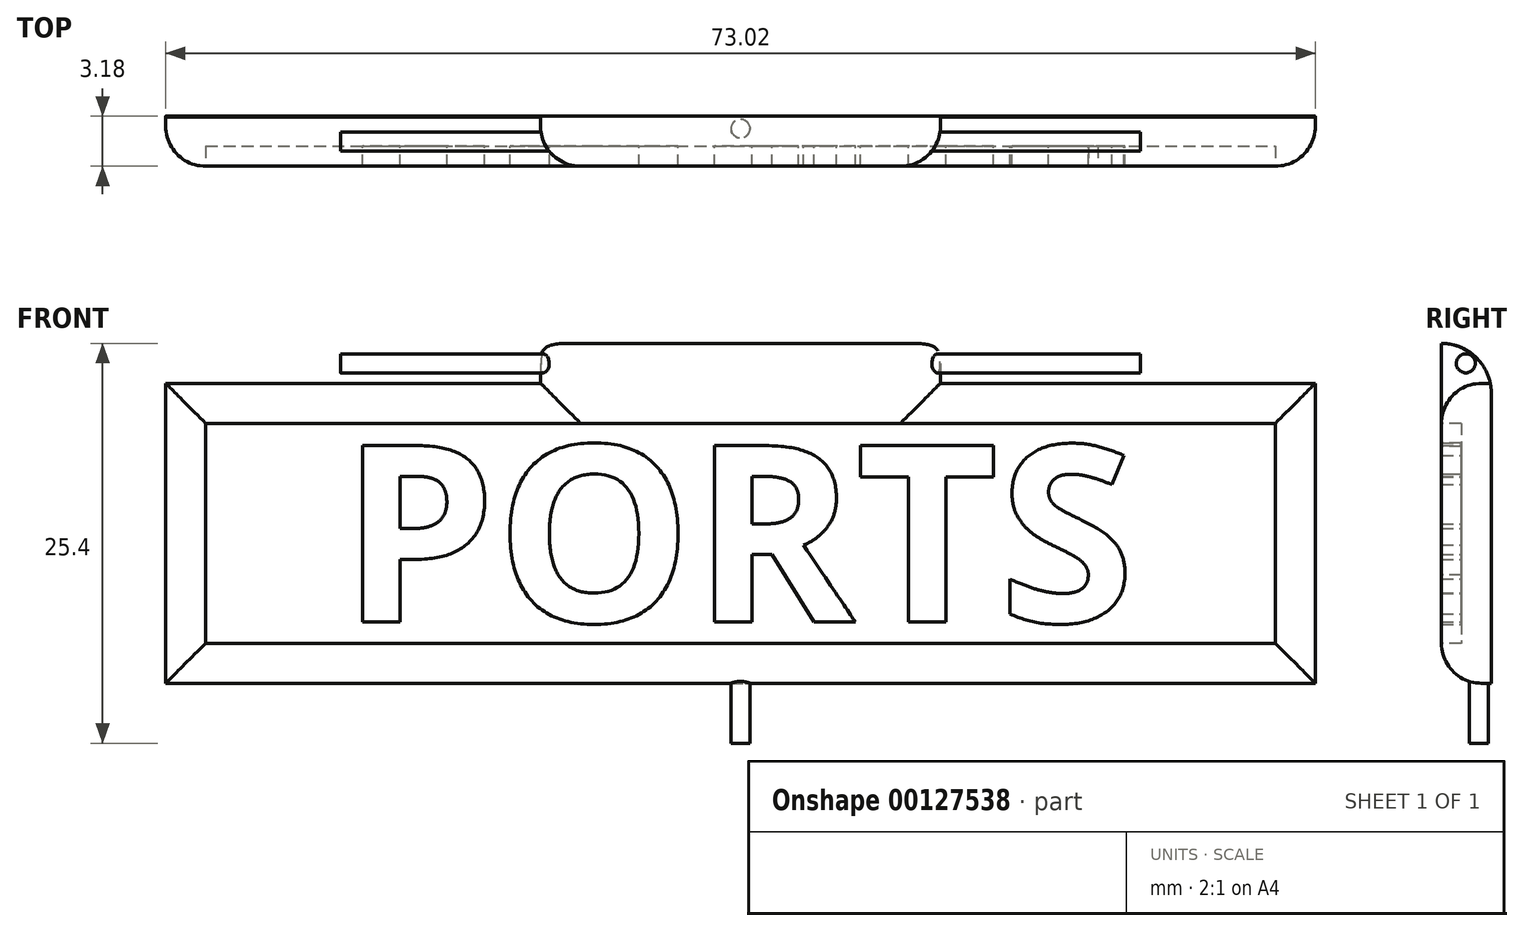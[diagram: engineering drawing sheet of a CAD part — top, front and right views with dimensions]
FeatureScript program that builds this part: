
annotation { "Feature Type Name" : "Feature", "Feature Type Description" : "" }
export const myFeature = defineFeature(function(context is Context, id is Id, definition is map)
    precondition{}
    {
        {
            var Q0;
            Q0=qCreatedBy(makeId("Front.planeOp"),FACE);
            var sketch = newSketch(context, id + "F0", { "sketchPlane" : qUnion([Q0])});
            skLineSegment(sketch, "E0.bottom", {"start": v(-57.71, 18) * mm, "end": v(15.31, 18) * mm});
            skLineSegment(sketch, "E0.top", {"start": v(-57.71, -1.06) * mm, "end": v(15.31, -1.06) * mm});
            skLineSegment(sketch, "E0.left", {"start": v(-57.71, 18) * mm, "end": v(-57.71, -1.06) * mm});
            skLineSegment(sketch, "E0.right", {"start": v(15.31, 18) * mm, "end": v(15.31, -1.06) * mm});
            skSolve(sketch);
        }
        {
            var Q0;
            Q0 = qSketchRegion(id + "F0", true);
            extrude(context, id + "F1", {"entities" : qUnion([Q0]), "depth" : 3.17 * mm});
        }
        {
            var Q0;
            Q0=makeQuery(id+"F1.opExtrude","SWEPT_FACE",FACE,{"disambiguationData":[OSD([sQuery(id+"F0.wireOp",EDGE,"E0.top")])]});
            var sketch = newSketch(context, id + "F2", { "sketchPlane" : qUnion([Q0])});
            skLineSegment(sketch, "E1", {"start": v(-57.71, 1.59) * mm, "end": v(-57.71, 0) * mm});
            skCircle(sketch, "E2", {"center": v(-21.2, 0.8) * mm, "radius": 0.6 * mm});
            skPoint(sketch, "E2.centerSnap0", {"position": v(-21.2, 0) * mm});
            skPoint(sketch, "E2.centerSnap1", {"position": v(-57.71, 0.8) * mm});
            skSolve(sketch);
        }
        {
            var Q0;
            Q0 = qSketchRegion(id + "F2", true);
            extrude(context, id + "F3", {"entities" : qUnion([Q0]), "operationType" : NewBodyOperationType.ADD, "depth" : 3.8 * mm});
        }
        {
            var Q0;
            Q0=makeQuery(id+"F1.opExtrude","SWEPT_FACE",FACE,{"disambiguationData":[OSD([sQuery(id+"F0.wireOp",EDGE,"E0.bottom")])]});
            var sketch = newSketch(context, id + "F4", { "sketchPlane" : qUnion([Q0])});
            skLineSegment(sketch, "E3.bottom", {"start": v(-33.9, -3.18) * mm, "end": v(-8.5, -3.18) * mm});
            skLineSegment(sketch, "E3.top", {"start": v(-33.9, 0) * mm, "end": v(-8.5, 0) * mm});
            skLineSegment(sketch, "E3.left", {"start": v(-33.9, -3.18) * mm, "end": v(-33.9, 0) * mm});
            skLineSegment(sketch, "E3.right", {"start": v(-8.5, -3.18) * mm, "end": v(-8.5, 0) * mm});
            skPoint(sketch, "E3.middle", {"position": v(-21.2, -1.59) * mm});
            skPoint(sketch, "E3.middle.positionSnap0", {"position": v(-21.2, -3.18) * mm});
            skPoint(sketch, "E3.middle.positionSnap1", {"position": v(15.31, -1.59) * mm});
            skPoint(sketch, "E3.centerSnap0", {"position": v(-21.2, -3.18) * mm});
            skPoint(sketch, "E3.centerSnap1", {"position": v(15.31, -1.59) * mm});
            skSolve(sketch);
        }
        {
            var Q0;
            Q0=makeQuery(id+"F4.imprint","IMPRINT",FACE,{"disambiguationData":[TD([[makeQuery(id+"F4.imprint","IMPRINT",EDGE,{"derivedFrom":sQuery(id+"F4.wireOp",EDGE,"E3.bottom")}),1.0]])]});
            extrude(context, id + "F5", {"entities" : qUnion([Q0]), "operationType" : NewBodyOperationType.ADD, "depth" : 2.54 * mm});
        }
        {
            var Q0;
            Q0=makeQuery(id+"F5.opExtrude","CAP_EDGE",EDGE,{"disambiguationData":[OSD([sQuery(id+"F4.wireOp",EDGE,"E3.top")])],"isStart":false});
            fillet(context, id + "F6", {"entities" : qUnion([Q0]), "radius" : 3.17 * mm, "tangentPropagation" : true, "allowEdgeOverflow" : false});
        }
        {
            var Q0;
            Q0=makeQuery(id+"F5.opExtrude","SWEPT_FACE",FACE,{"disambiguationData":[OSD([sQuery(id+"F4.wireOp",EDGE,"E3.right")])]});
            var sketch = newSketch(context, id + "F7", { "sketchPlane" : qUnion([Q0])});
            skCircle(sketch, "E4", {"center": v(-1.62, 19.26) * mm, "radius": 0.6 * mm});
            skPoint(sketch, "E4.centerSnap0", {"position": v(-1.62, 18) * mm});
            skPoint(sketch, "E4.centerSnap1", {"position": v(-3.18, 19.26) * mm});
            skSolve(sketch);
        }
        {
            var Q0;
            Q0 = qSketchRegion(id + "F7", true);
            extrude(context, id + "F8", {"entities" : qUnion([Q0]), "operationType" : NewBodyOperationType.ADD, "depth" : 12.7 * mm});
        }
        {
            var Q0;
            Q0=makeQuery(id+"F5.opExtrude","SWEPT_FACE",FACE,{"disambiguationData":[OSD([sQuery(id+"F4.wireOp",EDGE,"E3.left")])]});
            var sketch = newSketch(context, id + "F9", { "sketchPlane" : qUnion([Q0])});
            skCircle(sketch, "E5", {"center": v(1.62, 19.26) * mm, "radius": 0.6 * mm});
            skPoint(sketch, "E5.centerSnap0", {"position": v(1.62, 18) * mm});
            skPoint(sketch, "E5.centerSnap1", {"position": v(3.18, 19.26) * mm});
            skSolve(sketch);
        }
        {
            var Q0;
            Q0 = qSketchRegion(id + "F9", true);
            extrude(context, id + "F10", {"entities" : qUnion([Q0]), "operationType" : NewBodyOperationType.ADD, "depth" : 12.7 * mm});
        }
        {
            var Q0;
            Q0=makeQuery(id+"F1.opExtrude","CAP_EDGE",EDGE,{"disambiguationData":[OSD([sQuery(id+"F0.wireOp",EDGE,"E0.top")])],"isStart":false});
            var Q1;
            Q1=makeQuery(id+"F1.opExtrude","CAP_EDGE",EDGE,{"disambiguationData":[OSD([sQuery(id+"F0.wireOp",EDGE,"E0.right")])],"isStart":false});
            var Q2;
            {var subQ0=sQuery(id+"F0.wireOp",EDGE,"E0.right");var subQ1=sQuery(id+"F0.wireOp",EDGE,"E0.bottom");Q2=makeQuery(id+"F5.boolean.opBoolean","SPLIT",EDGE,{"disambiguationData":[TD([makeQuery(id+"F1.opExtrude","SWEPT_FACE",FACE,{"disambiguationData":[OSD([subQ0])]})])],"derivedFrom":makeQuery(id+"F1.opExtrude","CAP_EDGE",EDGE,{"disambiguationData":[OSD([subQ1])],"isStart":false})});}
            var Q3;
            Q3=makeQuery(id+"F1.opExtrude","CAP_EDGE",EDGE,{"disambiguationData":[OSD([sQuery(id+"F0.wireOp",EDGE,"E0.left")])],"isStart":false});
            var Q4;
            {var subQ0=sQuery(id+"F0.wireOp",EDGE,"E0.left");var subQ1=sQuery(id+"F0.wireOp",EDGE,"E0.bottom");Q4=makeQuery(id+"F5.boolean.opBoolean","SPLIT",EDGE,{"disambiguationData":[TD([makeQuery(id+"F1.opExtrude","SWEPT_FACE",FACE,{"disambiguationData":[OSD([subQ0])]})])],"derivedFrom":makeQuery(id+"F1.opExtrude","CAP_EDGE",EDGE,{"disambiguationData":[OSD([subQ1])],"isStart":false})});}
            var Q5;
            Q5=makeQuery(id+"F5.opExtrude","SWEPT_EDGE",EDGE,{"disambiguationData":[OSD([sQuery(id+"F0.wireOp",EDGE,"E0.bottom"),sQuery(id+"F4.wireOp",EDGE,"E3.bottom"),sQuery(id+"F4.wireOp",EDGE,"E3.right")])]});
            var Q6;
            Q6=makeQuery(id+"F5.opExtrude","SWEPT_EDGE",EDGE,{"disambiguationData":[OSD([sQuery(id+"F0.wireOp",EDGE,"E0.bottom"),sQuery(id+"F4.wireOp",EDGE,"E3.bottom"),sQuery(id+"F4.wireOp",EDGE,"E3.left")])]});
            fillet(context, id + "F11", {"entities" : qUnion([Q0, Q1, Q2, Q3, Q4, Q5, Q6]), "radius" : 2.54 * mm, "tangentPropagation" : true, "allowEdgeOverflow" : false});
        }
        {
            var Q0;
            Q0=makeQuery(id+"F5.boolean.opBoolean","MERGE",FACE,{"derivedFrom":[makeQuery(id+"F1.opExtrude","CAP_FACE",FACE,{"disambiguationData":[OSD([sQuery(id+"F0.wireOp",EDGE,"E0.bottom"),sQuery(id+"F0.wireOp",EDGE,"E0.top"),sQuery(id+"F0.wireOp",EDGE,"E0.left"),sQuery(id+"F0.wireOp",EDGE,"E0.right")])],"isStart":false}),makeQuery(id+"F5.opExtrude","SWEPT_FACE",FACE,{"disambiguationData":[OSD([sQuery(id+"F4.wireOp",EDGE,"E3.bottom")])]})]});
            var sketch = newSketch(context, id + "F12", { "sketchPlane" : qUnion([Q0])});
            skLineSegment(sketch, "E6.bottom", {"start": v(-55.17, 1.48) * mm, "end": v(12.77, 1.48) * mm});
            skLineSegment(sketch, "E6.top", {"start": v(-55.17, 15.45) * mm, "end": v(12.77, 15.45) * mm});
            skLineSegment(sketch, "E6.left", {"start": v(-55.17, 1.48) * mm, "end": v(-55.17, 15.45) * mm});
            skLineSegment(sketch, "E6.right", {"start": v(12.77, 1.48) * mm, "end": v(12.77, 15.45) * mm});
            skSolve(sketch);
        }
        {
            var Q0;
            Q0 = qSketchRegion(id + "F12", true);
            extrude(context, id + "F13", {"entities" : qUnion([Q0]), "operationType" : NewBodyOperationType.REMOVE, "oppositeDirection" : true, "depth" : 1.27 * mm});
        }
        {
            var Q0;
            Q0=makeQuery(id+"F13.boolean.opBoolean","COPY",FACE,{"derivedFrom":makeQuery(id+"F13.opExtrude","CAP_FACE",FACE,{"disambiguationData":[OSD([sQuery(id+"F12.wireOp",EDGE,"E6.bottom"),sQuery(id+"F12.wireOp",EDGE,"E6.top"),sQuery(id+"F12.wireOp",EDGE,"E6.left"),sQuery(id+"F12.wireOp",EDGE,"E6.right")])],"isStart":false})});
            var sketch = newSketch(context, id + "F14", { "sketchPlane" : qUnion([Q0])});
            skText(sketch, "E7", { "text": "PORTS", "fontName": "OpenSans-Bold.ttf"});
            const initialGuessF14  = {"E7": [-0.0466, 0.00283, 1, 0, 0.0113]};
            skSetInitialGuess(sketch, initialGuessF14);
            skSolve(sketch);
        }
        {
            var Q0;
            Q0 = qSketchRegion(id + "F14", true);
            extrude(context, id + "F15", {"entities" : qUnion([Q0]), "operationType" : NewBodyOperationType.ADD, "depth" : 1.27 * mm});
        }
    });
